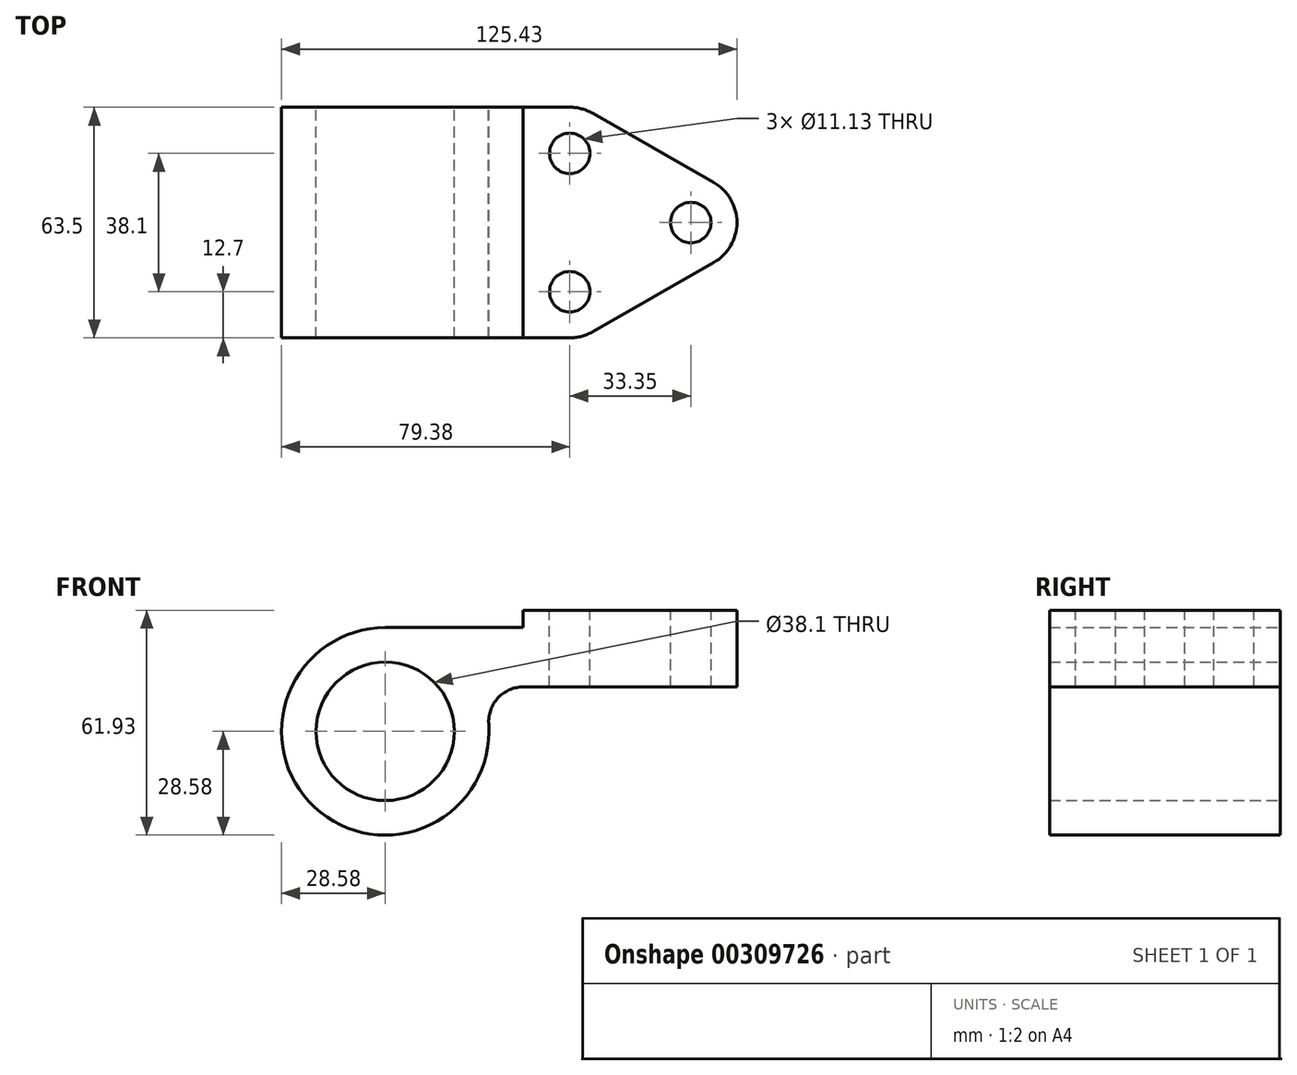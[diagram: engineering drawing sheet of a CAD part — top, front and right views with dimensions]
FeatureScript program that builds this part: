
annotation { "Feature Type Name" : "Feature", "Feature Type Description" : "" }
export const myFeature = defineFeature(function(context is Context, id is Id, definition is map)
    precondition{}
    {
        {
            var Q0;
            Q0=qCreatedBy(makeId("Front.planeOp"),FACE);
            var sketch = newSketch(context, id + "F0", { "sketchPlane" : qUnion([Q0])});
            skArc(sketch, "E0", {"start": v(0, 28.58) * mm, "mid": v(-19.47, -20.91) * mm, "end": v(28.5, 2.03) * mm});
            skArc(sketch, "E1", {"start": v(28.5, 2.03) * mm, "mid": v(31.03, 9.2) * mm, "end": v(38, 12.24) * mm});
            skLineSegment(sketch, "E2", {"start": v(38, 33.35) * mm, "end": v(38, 28.58) * mm});
            skLineSegment(sketch, "E3", {"start": v(38, 33.35) * mm, "end": v(101.7, 33.35) * mm});
            skLineSegment(sketch, "E4", {"start": v(38, 12.24) * mm, "end": v(101.7, 12.24) * mm});
            skLineSegment(sketch, "E5", {"start": v(101.7, 33.35) * mm, "end": v(101.7, 12.24) * mm});
            skLineSegment(sketch, "E6", {"start": v(38, 28.58) * mm, "end": v(0, 28.58) * mm});
            skCircle(sketch, "E7", {"center": v(0, 0) * mm, "radius": 19.05 * mm});
            skLineSegment(sketch, "E8", {"start": v(38, 28.58) * mm, "end": v(42.2, 28.58) * mm});
            skPoint(sketch, "E9", {"position": v(69.85, 12.24) * mm});
            skSolve(sketch);
        }
        {
            var Q0;
            Q0=makeQuery(id+"F0.imprint","IMPRINT",FACE,{"disambiguationData":[TD([[makeQuery(id+"F0.imprint","IMPRINT",EDGE,{"derivedFrom":sQuery(id+"F0.wireOp",EDGE,"E0")}),1.0]])]});
            extrude(context, id + "F1", {"entities" : qUnion([Q0]), "depth" : 63.5 * mm});
        }
        {
            var Q0;
            Q0=makeQuery(id+"F1.opExtrude","SWEPT_FACE",FACE,{"disambiguationData":[OSD([sQuery(id+"F0.wireOp",EDGE,"E3")])]});
            var sketch = newSketch(context, id + "F2", { "sketchPlane" : qUnion([Q0])});
            skCircle(sketch, "E10", {"center": v(50.8, -12.7) * mm, "radius": 5.56 * mm});
            skCircle(sketch, "E11", {"center": v(50.8, -50.8) * mm, "radius": 5.56 * mm});
            skPoint(sketch, "E12", {"position": v(50.8, -31.75) * mm});
            skPoint(sketch, "E13", {"position": v(84.15, -31.75) * mm});
            skCircle(sketch, "E14", {"center": v(84.15, -31.75) * mm, "radius": 5.56 * mm});
            skArc(sketch, "E15", {"start": v(90.45, -42.78) * mm, "mid": v(96.85, -31.75) * mm, "end": v(90.45, -20.72) * mm});
            skArc(sketch, "E16", {"start": v(57.1, -1.67) * mm, "mid": v(44.42, -1.72) * mm, "end": v(38.1, -12.7) * mm});
            skArc(sketch, "E17", {"start": v(38.1, -50.8) * mm, "mid": v(44.42, -61.78) * mm, "end": v(57.1, -61.83) * mm});
            skLineSegment(sketch, "E18", {"start": v(57.1, -1.67) * mm, "end": v(90.45, -20.72) * mm});
            skLineSegment(sketch, "E19", {"start": v(90.45, -42.78) * mm, "end": v(57.1, -61.83) * mm});
            skLineSegment(sketch, "E20", {"start": v(38.1, -12.7) * mm, "end": v(38.1, -50.8) * mm});
            skSolve(sketch);
        }
        {
            var Q0;
            Q0=makeQuery(id+"F2.imprint","IMPRINT",FACE,{"disambiguationData":[TD([[makeQuery(id+"F2.imprint","IMPRINT",EDGE,{"derivedFrom":sQuery(id+"F2.wireOp",EDGE,"E15")}),-1.0]])]});
            var Q1;
            Q1=makeQuery(id+"F2.imprint","IMPRINT",FACE,{"disambiguationData":[TD([[makeQuery(id+"F2.imprint","IMPRINT",EDGE,{"derivedFrom":sQuery(id+"F2.wireOp",EDGE,"E11")}),1.0]])]});
            var Q2;
            Q2=makeQuery(id+"F2.imprint","IMPRINT",FACE,{"disambiguationData":[TD([[makeQuery(id+"F2.imprint","IMPRINT",EDGE,{"derivedFrom":sQuery(id+"F2.wireOp",EDGE,"E14")}),1.0]])]});
            var Q3;
            Q3=makeQuery(id+"F2.imprint","IMPRINT",FACE,{"disambiguationData":[TD([[makeQuery(id+"F2.imprint","IMPRINT",EDGE,{"derivedFrom":sQuery(id+"F2.wireOp",EDGE,"E10")}),1.0]])]});
            extrude(context, id + "F3", {"entities" : qUnion([Q0, Q1, Q2, Q3]), "operationType" : NewBodyOperationType.REMOVE, "oppositeDirection" : true, "depth" : 25.4 * mm});
        }
    });
